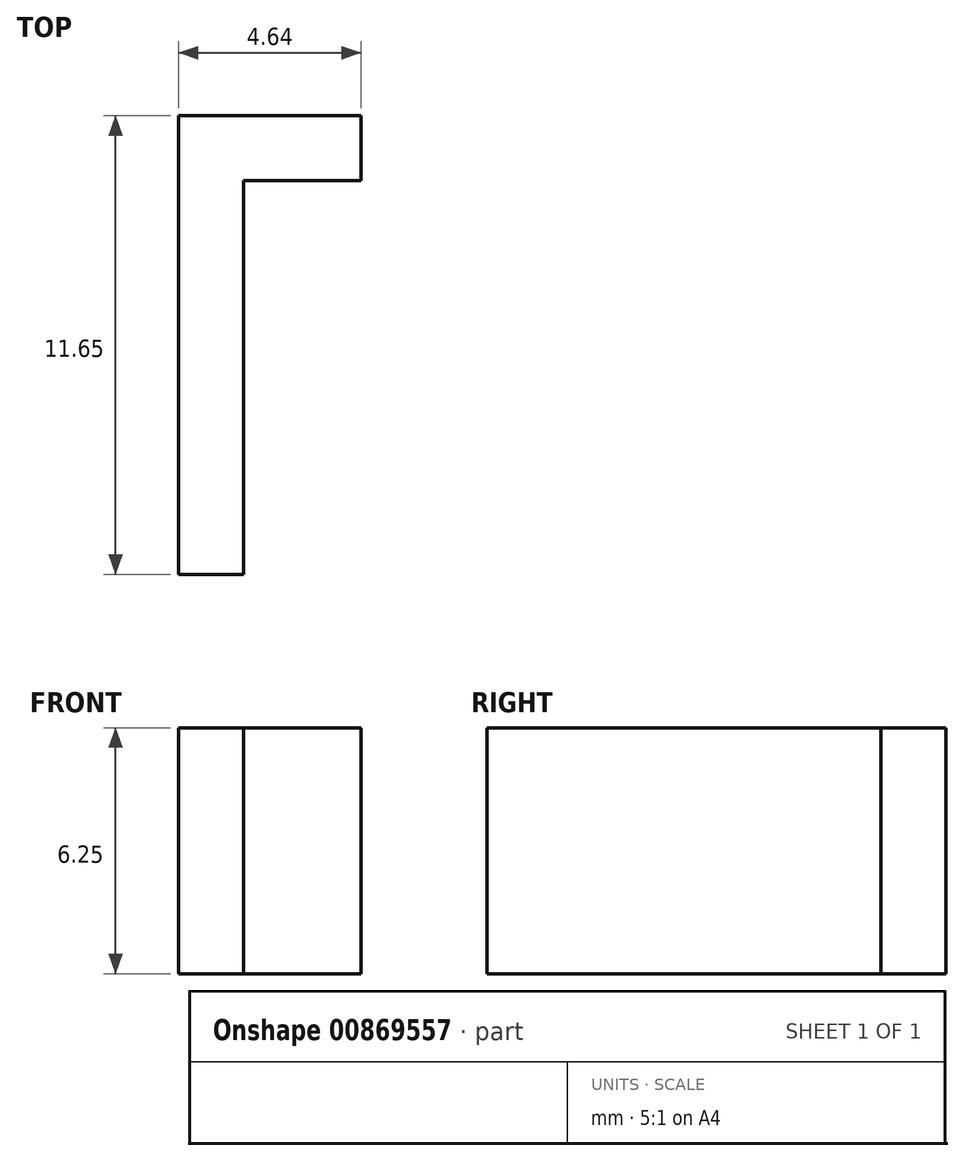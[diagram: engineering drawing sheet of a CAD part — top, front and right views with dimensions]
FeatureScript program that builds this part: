
annotation { "Feature Type Name" : "Feature", "Feature Type Description" : "" }
export const myFeature = defineFeature(function(context is Context, id is Id, definition is map)
    precondition{}
    {
        {
            var Q0;
            Q0=qCreatedBy(makeId("Top.planeOp"), FACE);
            var sketch = newSketch(context, id + "F0", { "sketchPlane" : qUnion([Q0])});
            skLineSegment(sketch, "E0", {"start": v(0, 0) * mm, "end": v(0, 11.65) * mm});
            skLineSegment(sketch, "E1", {"start": v(0, 11.65) * mm, "end": v(4.64, 11.65) * mm});
            skLineSegment(sketch, "E2", {"start": v(4.64, 11.65) * mm, "end": v(4.64, 10) * mm});
            skLineSegment(sketch, "E3", {"start": v(4.64, 10) * mm, "end": v(1.65, 10) * mm});
            skLineSegment(sketch, "E4", {"start": v(1.65, 10) * mm, "end": v(1.65, 0) * mm});
            skLineSegment(sketch, "E5", {"start": v(1.65, 0) * mm, "end": v(0, 0) * mm});
            skSolve(sketch);
        }
        {
            var Q0;
            Q0 = qSketchRegion(id + "F0", true);
            extrude(context, id + "F1", {"entities" : qUnion([Q0]), "depth" : 6.25 * mm, "offsetDistance" : 25 * mm});
        }
    });
